# Revit family: Gravity_Hoods-Ventilation-Carnes-GSAA
name_source: partatom
category: Mechanical Equipment
revit_build: Autodesk Revit MEP 2012 (Build: 20110309_2315(x64)
units: mm (PartAtom-declared; Revit-internal decimal feet)

## types (9) — shared parameters
04 CSI = 23 34 23
95 CSI = 15830
Assembly Code = D3040200
Catalog URL = http://www.carnes.com
Default Elevation = 0"
Description = Non-Powered Ventilators
Flow Rate = 0.0 L/s
Manufacturer = CARNES COMPANY
Manufacturer Fax = 608-845-6470
Material = Spun Aluminum
Product Page URL = http://www.carnes.com
Spec Sheet URL = http://www.carnes.com
Subcategory = Ventilation
URL = http://www.carnes.com
Unit = Aluminum - Carnes - Brushed
ecoScorecard Product Page = http://ecoscorecard.com

## per-type parameters (varying)
| type | A | C | E | F | G | Inlet Area Sq.Ft. | Throat Area Dia. | Throat Area Sq.Ft. |
| GSAA 12 | 21 3/4" | 20 1/2" | 3 1/2" | 16" | 8 7/8" | 1 159/256" | 13 1/4" | 123/128" |
| GSAA 16 | 25 3/4" | 25" | 3" | 20" | 10 1/4" | 2 59/256" | 16 1/4" | 1 113/256" |
| GSAA 22 | 33 1/8" | 28 1/2" | 4 1/4" | 24" | 12 1/4" | 3 87/256" | 22" | 2 41/64" |
| GSAA 28 | 42 1/4" | 37" | 3 1/2" | 32" | 13 5/8" | 5 59/256" | 28 3/4" | 4 131/256" |
| GSAA 32 | 50 1/4" | 43" | 5" | 38" | 18 3/8" | 8 49/256" | 32" | 5 37/64" |
| GSAA 38 | 57 1/2" | 49" | 6 1/2" | 44" | 21 1/8" | 10 41/256" | 38" | 7 223/256" |
| GSAA 46 | 68 1/4" | 57" | 6 7/8" | 52" | 25 1/2" | 13 55/64" | 46" | 11 69/128" |
| GSAA 52 | 78 1/2" | 57" | 10 1/2" | 52" | 30 1/4" | 18 55/64" | 52" | 14 3/4" |
| GSAA 60 | 84 3/4" | 67" | 12 1/2" | 62" | 32 1/4" | 19 41/64" | 60" | 19 41/64" |

note: column(s) folded — value = type name in every type: Model

## geometry (parser evidence)
native form markers: Blend x1, Sweep x6
no freeform markers — native parametric forms only
